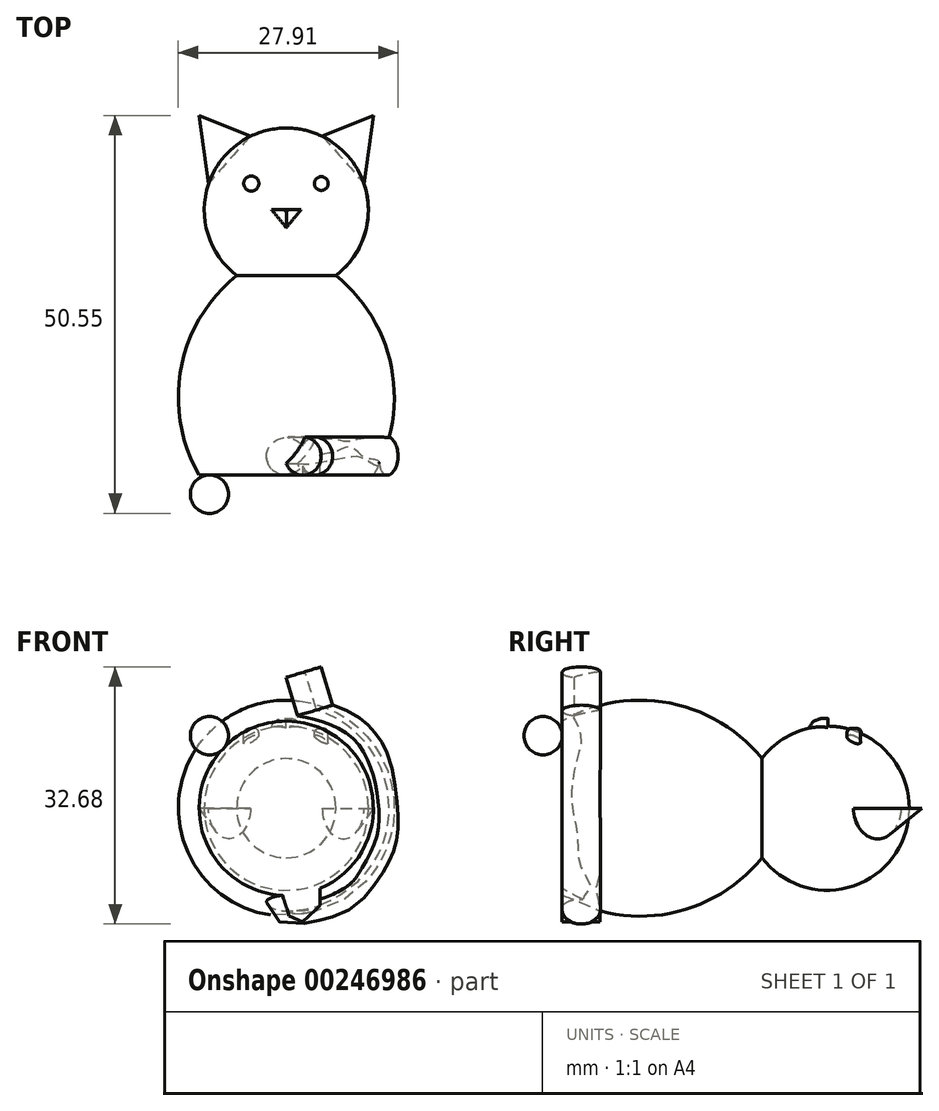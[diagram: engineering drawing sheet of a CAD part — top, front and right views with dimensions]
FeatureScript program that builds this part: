
annotation { "Feature Type Name" : "Feature", "Feature Type Description" : "" }
export const myFeature = defineFeature(function(context is Context, id is Id, definition is map)
    precondition{}
    {
        {
            var Q0;
            Q0=qCreatedBy(makeId("Top.planeOp"),FACE);
            var sketch = newSketch(context, id + "F0", { "sketchPlane" : qUnion([Q0])});
            skArc(sketch, "E0", {"start": v(6.3, 25.37) * mm, "mid": v(9.88, 37) * mm, "end": v(0, 44.1) * mm});
            skLineSegment(sketch, "E1", {"start": v(0, 0) * mm, "end": v(0, 50.8) * mm});
            skArc(sketch, "E2", {"start": v(11.06, 0) * mm, "mid": v(13.38, 13.57) * mm, "end": v(6.3, 25.37) * mm});
            skLineSegment(sketch, "E3", {"start": v(11.06, 0) * mm, "end": v(0, 0) * mm});
            skSolve(sketch);
        }
        {
            var Q0;
            {var subQ0=sQuery(id+"F0.wireOp",EDGE,"E0");Q0=makeQuery(id+"F0.imprint","IMPRINT",FACE,{"disambiguationData":[TD([[makeQuery(id+"F0.imprint","IMPRINT",EDGE,{"derivedFrom":subQ0}),1.0]])]});}
            var Q1;
            Q1=sQuery(id+"F0.wireOp",EDGE,"E1");
            revolve(context, id + "F1", {"entities" : qUnion([Q0]), "axis" : qUnion([Q1]), "revolveType" : RevolveType.FULL});
        }
        {
            var Q0;
            Q0=qCreatedBy(makeId("Top.planeOp"),FACE);
            var sketch = newSketch(context, id + "F2", { "sketchPlane" : qUnion([Q0])});
            skLineSegment(sketch, "E4", {"start": v(0, 0) * mm, "end": v(0, 50.8) * mm});
            skSolve(sketch);
        }
        {
            var Q0;
            Q0=qCreatedBy(makeId("Top.planeOp"),FACE);
            var sketch = newSketch(context, id + "F3", { "sketchPlane" : qUnion([Q0])});
            skLineSegment(sketch, "E5", {"start": v(6.2, 39.42) * mm, "end": v(2.57, 42.24) * mm});
            skLineSegment(sketch, "E6", {"start": v(2.57, 42.24) * mm, "end": v(11.07, 45.7) * mm});
            skLineSegment(sketch, "E7", {"start": v(6.2, 39.42) * mm, "end": v(11.07, 45.7) * mm});
            skPoint(sketch, "E8.orphan", {"position": v(9.82, 36.61) * mm});
            skLineSegment(sketch, "E9.MirrorCS", {"start": v(-2.57, 42.24) * mm, "end": v(-11.07, 45.7) * mm});
            skLineSegment(sketch, "E10.MirrorCS", {"start": v(-6.2, 39.42) * mm, "end": v(-2.57, 42.24) * mm});
            skLineSegment(sketch, "E11.MirrorCS", {"start": v(-6.2, 39.42) * mm, "end": v(-11.07, 45.7) * mm});
            skSolve(sketch);
        }
        {
            var Q0;
            Q0=makeQuery(id+"F3.imprint","IMPRINT",FACE,{"disambiguationData":[TD([[makeQuery(id+"F3.imprint","IMPRINT",EDGE,{"derivedFrom":sQuery(id+"F3.wireOp",EDGE,"E5")}),-1.0]])]});
            var Q1;
            Q1=sQuery(id+"F3.wireOp",EDGE,"E7");
            revolve(context, id + "F4", {"operationType" : NewBodyOperationType.ADD, "entities" : qUnion([Q0]), "axis" : qUnion([Q1]), "revolveType" : RevolveType.ONE_DIRECTION, "oppositeDirection" : true, "angle" : 180 * degree});
        }
        {
            var Q0;
            Q0=makeQuery(id+"F3.imprint","IMPRINT",FACE,{"disambiguationData":[TD([[makeQuery(id+"F3.imprint","IMPRINT",EDGE,{"derivedFrom":sQuery(id+"F3.wireOp",EDGE,"E9.MirrorCS")}),1.0]])]});
            var Q1;
            Q1=sQuery(id+"F3.wireOp",EDGE,"E11.MirrorCS");
            revolve(context, id + "F5", {"operationType" : NewBodyOperationType.ADD, "entities" : qUnion([Q0]), "axis" : qUnion([Q1]), "revolveType" : RevolveType.ONE_DIRECTION, "angle" : 180 * degree});
        }
        {
            var Q0;
            Q0=qCreatedBy(makeId("Top.planeOp"),FACE);
            cPlane(context, id + "F6", {"entities" : qUnion([Q0]), "cplaneType" : CPlaneType.OFFSET, "offset" : 10.16 * mm, "width" : 152.4 * mm, "height" : 152.4 * mm});
        }
        {
            var Q0;
            Q0=qCreatedBy(id+"F6.planeOp",FACE);
            var sketch = newSketch(context, id + "F7", { "sketchPlane" : qUnion([Q0])});
            skCircle(sketch, "E12", {"center": v(4.45, 37.05) * mm, "radius": 0.87 * mm});
            skCircle(sketch, "E13", {"center": v(-4.45, 37.05) * mm, "radius": 0.96 * mm});
            skLineSegment(sketch, "E14", {"start": v(0, 31.45) * mm, "end": v(-1.87, 33.74) * mm});
            skLineSegment(sketch, "E15", {"start": v(-1.87, 33.74) * mm, "end": v(1.9, 33.74) * mm});
            skLineSegment(sketch, "E16", {"start": v(1.9, 33.74) * mm, "end": v(0, 31.45) * mm});
            skSolve(sketch);
        }
        {
            var Q0;
            Q0=makeQuery(id+"F7.imprint","IMPRINT",FACE,{"disambiguationData":[TD([[makeQuery(id+"F7.imprint","IMPRINT",EDGE,{"derivedFrom":sQuery(id+"F7.wireOp",EDGE,"E13")}),1.0]])]});
            var Q1;
            Q1=makeQuery(id+"F7.imprint","IMPRINT",FACE,{"disambiguationData":[TD([[makeQuery(id+"F7.imprint","IMPRINT",EDGE,{"derivedFrom":sQuery(id+"F7.wireOp",EDGE,"E12")}),1.0]])]});
            extrude(context, id + "F8", {"entities" : qUnion([Q0, Q1]), "operationType" : NewBodyOperationType.ADD, "oppositeDirection" : true, "depth" : 12.7 * mm});
        }
        {
            var Q0;
            Q0=makeQuery(id+"F8.opExtrude","CAP_EDGE",EDGE,{"disambiguationData":[OSD([sQuery(id+"F7.wireOp",EDGE,"E13")])],"isStart":true});
            var Q1;
            Q1=makeQuery(id+"F8.opExtrude","CAP_EDGE",EDGE,{"disambiguationData":[OSD([sQuery(id+"F7.wireOp",EDGE,"E12")])],"isStart":true});
            fillet(context, id + "F9", {"entities" : qUnion([Q0, Q1]), "radius" : 0.64 * mm, "tangentPropagation" : true, "allowEdgeOverflow" : false});
        }
        {
            var Q0;
            Q0=makeQuery(id+"F7.imprint","IMPRINT",FACE,{"disambiguationData":[TD([[makeQuery(id+"F7.imprint","IMPRINT",EDGE,{"derivedFrom":sQuery(id+"F7.wireOp",EDGE,"E14")}),-1.0]])]});
            extrude(context, id + "F10", {"entities" : qUnion([Q0]), "operationType" : NewBodyOperationType.ADD, "depth" : 1.27 * mm});
        }
        {
            var Q0;
            Q0=makeQuery(id+"F10.opExtrude","CAP_EDGE",EDGE,{"disambiguationData":[OSD([sQuery(id+"F7.wireOp",EDGE,"E16")])],"isStart":false});
            var Q1;
            Q1=makeQuery(id+"F10.opExtrude","CAP_EDGE",EDGE,{"disambiguationData":[OSD([sQuery(id+"F7.wireOp",EDGE,"E14")])],"isStart":false});
            fillet(context, id + "F11", {"entities" : qUnion([Q0, Q1]), "radius" : 1.27 * mm, "tangentPropagation" : true, "allowEdgeOverflow" : false});
        }
        {
            var Q0;
            Q0=makeQuery(id+"F1.opRevolve","SWEPT_FACE",FACE,{"disambiguationData":[OSD([sQuery(id+"F0.wireOp",EDGE,"E3")])]});
            var sketch = newSketch(context, id + "F12", { "sketchPlane" : qUnion([Q0])});
            skFitSpline(sketch, "E17", {"points": [v(0, -10.54) * mm, v(0, -13.13) * mm, v(5.16, -13.26) * mm, v(10.8, -9.5) * mm, v(14.02, -3.01) * mm, v(13.08, 5.9) * mm, v(8.87, 11.45) * mm, v(3.14, 13.15) * mm, v(2.75, 10.72) * mm, v(7.32, 8.3) * mm, v(9.6, 5.5) * mm, v(10.97, 1.46) * mm, v(10.57, -3.27) * mm, v(8.67, -6.88) * mm, v(4.91, -9.91) * mm, v(0, -10.54) * mm]});
            skSolve(sketch);
        }
        {
            var Q0;
            {var subQ0=sQuery(id+"F12.wireOp",EDGE,"E17");var subQ1=makeQuery(id+"F1.opRevolve","SWEPT_EDGE",EDGE,{"disambiguationData":[OSD([sQuery(id+"F0.wireOp",EDGE,"E2"),sQuery(id+"F0.wireOp",EDGE,"E3")])]});var subQ8=makeQuery(id+"F12.imprint","INTERSECT",VERTEX,{"disambiguationData":[OD(0.0)],"derivedFrom":[subQ1,subQ0]});Q0=makeQuery(id+"F12.imprint","IMPRINT",FACE,{"disambiguationData":[TD([[makeQuery(id+"F12.imprint","IMPRINT",EDGE,{"disambiguationData":[TD([[subQ8,-1.0]])],"derivedFrom":subQ0}),-1.0]])]});}
            var sketch = newSketch(context, id + "F13", { "sketchPlane" : qUnion([Q0])});
            skFitSpline(sketch, "E18", {"points": [v(0, -10.51) * mm, v(0.52, -12.7) * mm, v(6.49, -11.62) * mm, v(9.84, -8.77) * mm, v(12.12, -4.36) * mm, v(12.48, 0.43) * mm, v(10.5, 7.6) * mm, v(6.4, 11.17) * mm, v(3.07, 12.24) * mm], "startDerivative": vector(-2.23, -31.48) * mm, "endDerivative": vector(-30.18, 7.36) * mm});
            skSolve(sketch);
        }
        {
            var Q0;
            Q0=qCreatedBy(makeId("Top.planeOp"),FACE);
            cPlane(context, id + "F14", {"entities" : qUnion([Q0]), "cplaneType" : CPlaneType.OFFSET, "offset" : 12.7 * mm, "oppositeDirection" : true, "width" : 152.4 * mm, "height" : 152.4 * mm});
        }
        {
            var Q0;
            Q0=qCreatedBy(id+"F14.planeOp",FACE);
            var sketch = newSketch(context, id + "F15", { "sketchPlane" : qUnion([Q0])});
            skCircle(sketch, "E19", {"center": v(0, 2.43) * mm, "radius": 2.43 * mm});
            skSolve(sketch);
        }
        {
            var Q0;
            Q0=makeQuery(id+"F15.imprint","IMPRINT",FACE,{"disambiguationData":[TD([[makeQuery(id+"F15.imprint","IMPRINT",EDGE,{"derivedFrom":sQuery(id+"F15.wireOp",EDGE,"E19")}),1.0]])]});
            var Q1;
            Q1=sQuery(id+"F13.wireOp",EDGE,"E18");
            sweep(context, id + "F16", {"operationType" : NewBodyOperationType.ADD, "profiles" : qUnion([Q0]), "path" : qUnion([Q1])});
        }
        {
            var Q0;
            Q0=makeQuery(id+"F16.opSweep","CAP_FACE",FACE,{"disambiguationData":[OSD([sQuery(id+"F13.wireOp",VERTEX,"E18.end"),sQuery(id+"F15.wireOp",EDGE,"E19")])],"isStart":false});
            var sketch = newSketch(context, id + "F17", { "sketchPlane" : qUnion([Q0])});
            skLineSegment(sketch, "E20", {"start": v(-0.41, 11.23) * mm, "end": v(-4.44, 13.94) * mm});
            skArc(sketch, "E21", {"start": v(-0.41, 11.23) * mm, "mid": v(-1.07, 14.6) * mm, "end": v(-4.44, 13.94) * mm});
            skSolve(sketch);
        }
        {
            var Q0;
            Q0=makeQuery(id+"F16.opSweep","CAP_FACE",FACE,{"disambiguationData":[OSD([sQuery(id+"F13.wireOp",VERTEX,"E18.start"),sQuery(id+"F15.wireOp",EDGE,"E19")])],"isStart":true});
            extrude(context, id + "F18", {"entities" : qUnion([Q0]), "operationType" : NewBodyOperationType.ADD, "depth" : 5.08 * mm});
        }
        {
            var Q0;
            Q0=makeQuery(id+"F1.opRevolve","SWEPT_FACE",FACE,{"disambiguationData":[OSD([sQuery(id+"F0.wireOp",EDGE,"E3")])]});
            var sketch = newSketch(context, id + "F19", { "sketchPlane" : qUnion([Q0])});
            skLineSegment(sketch, "E22", {"start": v(-1.08, -9.17) * mm, "end": v(0.36, -13.7) * mm});
            skLineSegment(sketch, "E23", {"start": v(0.36, -13.7) * mm, "end": v(2.08, -14.41) * mm});
            skLineSegment(sketch, "E24", {"start": v(2.08, -14.41) * mm, "end": v(4.3, -12.33) * mm});
            skLineSegment(sketch, "E25", {"start": v(4.3, -12.33) * mm, "end": v(4.3, -9.37) * mm});
            skLineSegment(sketch, "E26", {"start": v(4.3, -9.37) * mm, "end": v(-1.08, -9.17) * mm});
            skSolve(sketch);
        }
        {
            var Q0;
            {var subQ5=sQuery(id+"F19.wireOp",EDGE,"E23");Q0=makeQuery(id+"F19.imprint","IMPRINT",FACE,{"disambiguationData":[TD([[makeQuery(id+"F19.imprint","IMPRINT",EDGE,{"derivedFrom":subQ5}),1.0]])]});}
            extrude(context, id + "F20", {"entities" : qUnion([Q0]), "operationType" : NewBodyOperationType.ADD, "oppositeDirection" : true, "depth" : 4.83 * mm});
        }
        {
            var Q0;
            Q0=makeQuery(id+"F17.imprint","IMPRINT",FACE,{"disambiguationData":[TD([[makeQuery(id+"F17.imprint","IMPRINT",EDGE,{"derivedFrom":sQuery(id+"F17.wireOp",EDGE,"E20")}),-1.0]])]});
            var Q1;
            Q1=sQuery(id+"F17.wireOp",EDGE,"E20");
            revolve(context, id + "F21", {"operationType" : NewBodyOperationType.ADD, "entities" : qUnion([Q0]), "axis" : qUnion([Q1]), "revolveType" : RevolveType.FULL});
        }
    });
